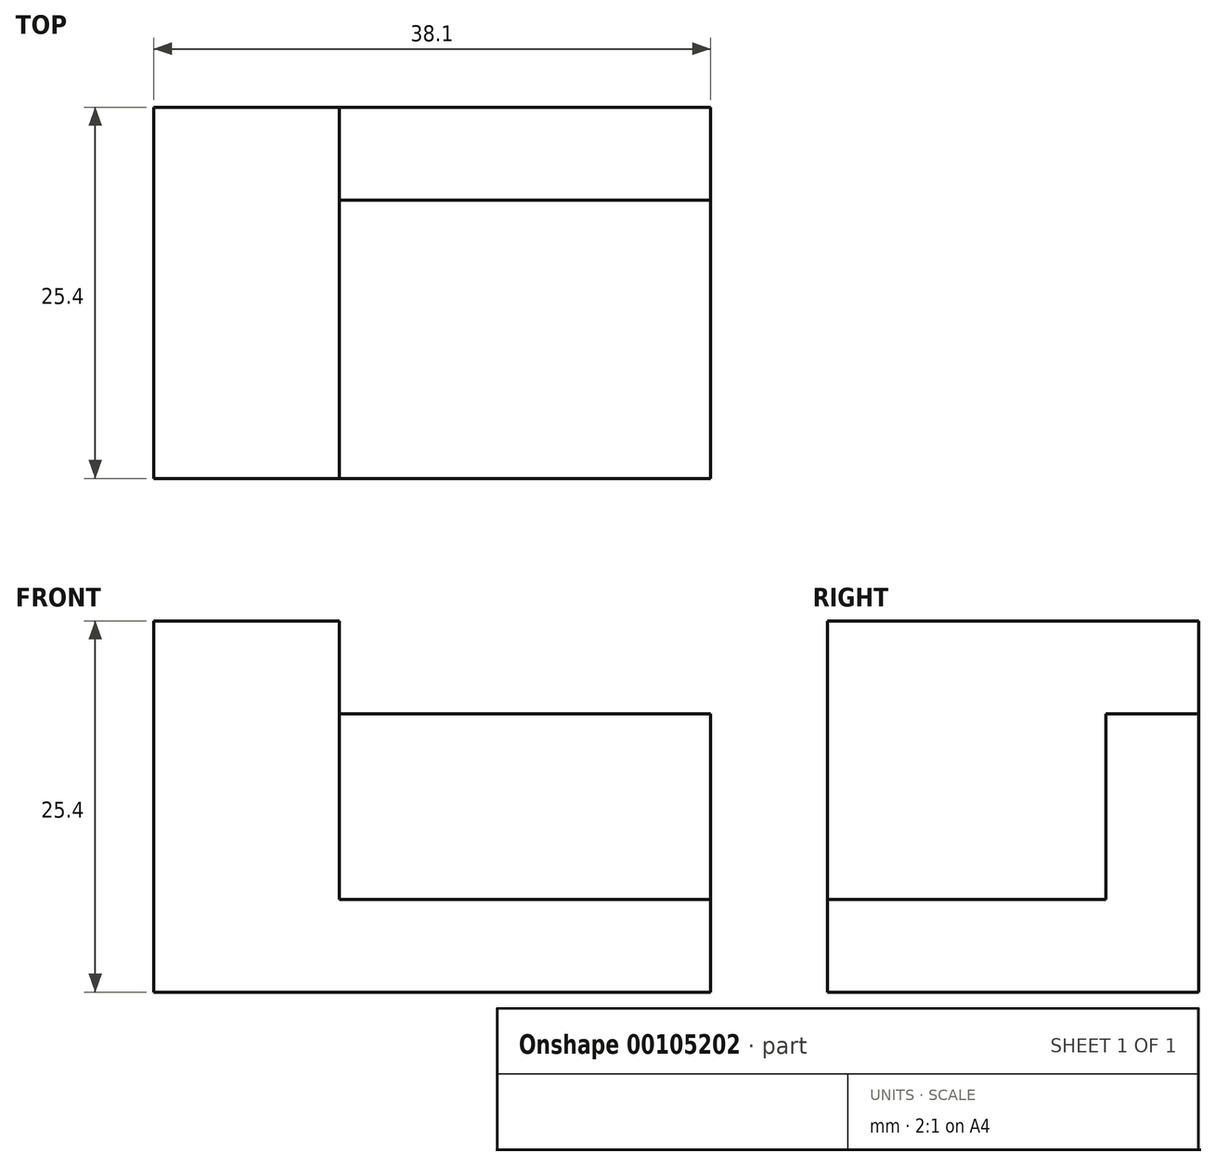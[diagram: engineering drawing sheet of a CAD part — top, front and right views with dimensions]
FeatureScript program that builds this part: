
annotation { "Feature Type Name" : "Feature", "Feature Type Description" : "" }
export const myFeature = defineFeature(function(context is Context, id is Id, definition is map)
    precondition{}
    {
        {
            var Q0;
            Q0=qCreatedBy(makeId("Front.planeOp"),FACE);
            var sketch = newSketch(context, id + "F0", { "sketchPlane" : qUnion([Q0])});
            skLineSegment(sketch, "E0.bottom", {"start": v(0, 0) * mm, "end": v(-38.1, 0) * mm});
            skLineSegment(sketch, "E0.top", {"start": v(0, 25.4) * mm, "end": v(-38.1, 25.4) * mm});
            skLineSegment(sketch, "E0.left", {"start": v(0, 0) * mm, "end": v(0, 25.4) * mm});
            skLineSegment(sketch, "E0.right", {"start": v(-38.1, 0) * mm, "end": v(-38.1, 25.4) * mm});
            skSolve(sketch);
        }
        {
            var Q0;
            Q0 = qSketchRegion(id + "F0", true);
            extrude(context, id + "F1", {"entities" : qUnion([Q0]), "endBound" : BoundingType.SYMMETRIC, "depth" : 25.4 * mm});
        }
        {
            var Q0;
            Q0=qCreatedBy(makeId("Front.planeOp"),FACE);
            var sketch = newSketch(context, id + "F2", { "sketchPlane" : qUnion([Q0])});
            skLineSegment(sketch, "E1.bottom", {"start": v(0, 6.35) * mm, "end": v(-25.4, 6.35) * mm});
            skLineSegment(sketch, "E1.top", {"start": v(0, 25.4) * mm, "end": v(-25.4, 25.4) * mm});
            skLineSegment(sketch, "E1.left", {"start": v(0, 6.35) * mm, "end": v(0, 25.4) * mm});
            skLineSegment(sketch, "E1.right", {"start": v(-25.4, 6.35) * mm, "end": v(-25.4, 25.4) * mm});
            skSolve(sketch);
        }
        {
            var Q0;
            Q0 = qSketchRegion(id + "F2", true);
            extrude(context, id + "F3", {"entities" : qUnion([Q0]), "operationType" : NewBodyOperationType.REMOVE, "depth" : 12.7 * mm, "hasSecondDirection" : true, "secondDirectionOppositeDirection" : true, "secondDirectionDepth" : 6.35 * mm});
        }
        {
            var Q0;
            Q0=qCreatedBy(makeId("Front.planeOp"),FACE);
            var sketch = newSketch(context, id + "F4", { "sketchPlane" : qUnion([Q0])});
            skLineSegment(sketch, "E2.bottom", {"start": v(-25.4, 25.4) * mm, "end": v(0, 25.4) * mm});
            skLineSegment(sketch, "E2.top", {"start": v(-25.4, 19.05) * mm, "end": v(0, 19.05) * mm});
            skLineSegment(sketch, "E2.left", {"start": v(-25.4, 25.4) * mm, "end": v(-25.4, 19.05) * mm});
            skLineSegment(sketch, "E2.right", {"start": v(0, 25.4) * mm, "end": v(0, 19.05) * mm});
            skSolve(sketch);
        }
        {
            var Q0;
            Q0 = qSketchRegion(id + "F4", true);
            extrude(context, id + "F5", {"entities" : qUnion([Q0]), "operationType" : NewBodyOperationType.REMOVE, "oppositeDirection" : true, "depth" : 25.4 * mm});
        }
    });
